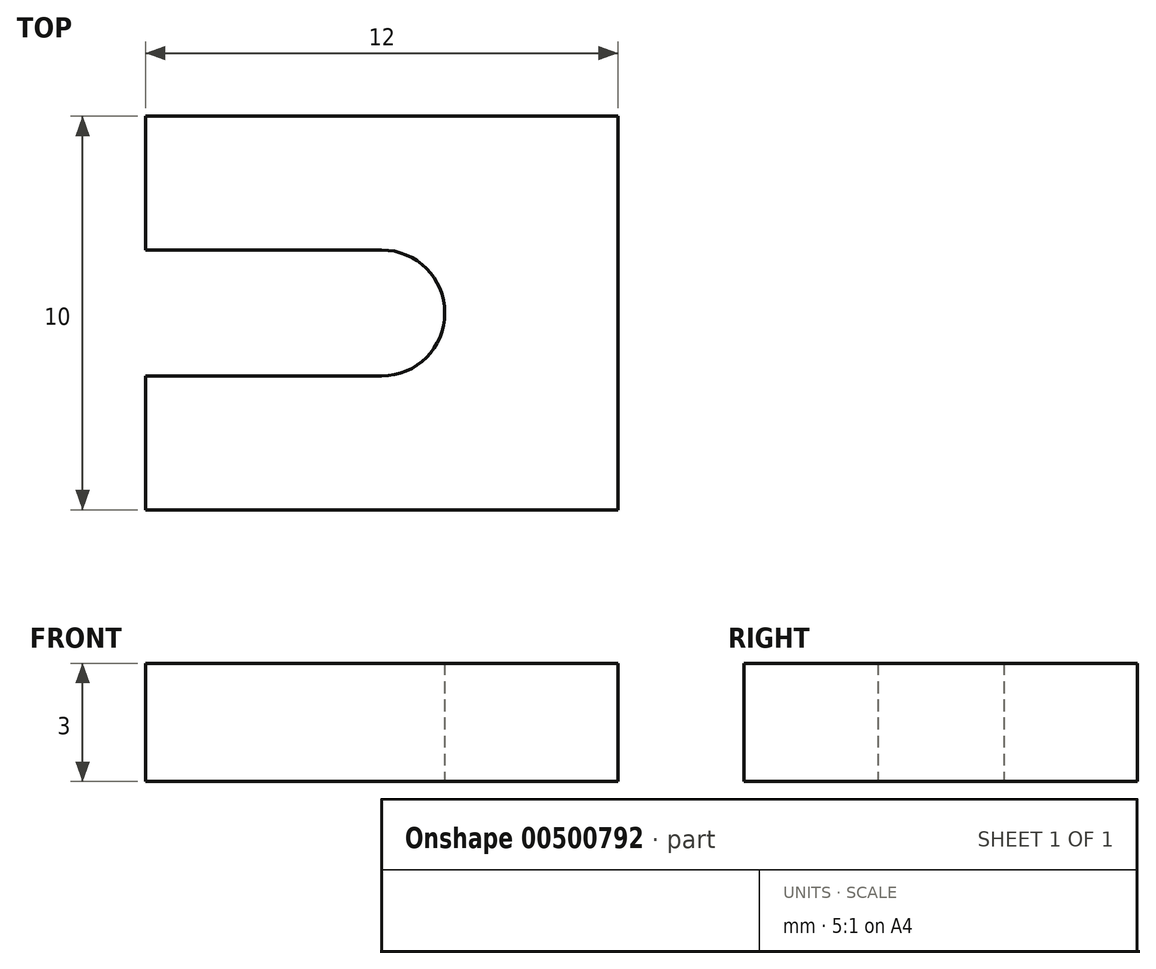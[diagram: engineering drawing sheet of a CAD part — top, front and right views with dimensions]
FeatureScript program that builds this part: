
annotation { "Feature Type Name" : "Feature", "Feature Type Description" : "" }
export const myFeature = defineFeature(function(context is Context, id is Id, definition is map)
    precondition{}
    {
        {
            var Q0;
            Q0=qCreatedBy(makeId("Top.planeOp"),FACE);
            var sketch = newSketch(context, id + "F0", { "sketchPlane" : qUnion([Q0])});
            skLineSegment(sketch, "E0.bottom", {"start": v(6, 5) * mm, "end": v(-6, 5) * mm});
            skLineSegment(sketch, "E0.top", {"start": v(6, -5) * mm, "end": v(-6, -5) * mm});
            skLineSegment(sketch, "E0.left", {"start": v(6, 5) * mm, "end": v(6, -5) * mm});
            skLineSegment(sketch, "E0.right", {"start": v(-6, 5) * mm, "end": v(-6, -5) * mm});
            skPoint(sketch, "E0.middle", {"position": v(0, 0) * mm});
            skCircle(sketch, "E1", {"center": v(0, 0) * mm, "radius": 1.6 * mm});
            skLineSegment(sketch, "E2", {"start": v(0, -1.6) * mm, "end": v(-6, -1.6) * mm});
            skLineSegment(sketch, "E3", {"start": v(-6, -1.6) * mm, "end": v(0, -1.6) * mm});
            skLineSegment(sketch, "E4", {"start": v(0, -1.6) * mm, "end": v(6, -1.6) * mm});
            skLineSegment(sketch, "E5", {"start": v(0, 1.6) * mm, "end": v(-6, 1.6) * mm});
            skLineSegment(sketch, "E6", {"start": v(0, 1.6) * mm, "end": v(6, 1.6) * mm});
            skSolve(sketch);
        }
        {
            var Q0;
            Q0=makeQuery(id+"F0.imprint","IMPRINT",FACE,{"disambiguationData":[TD([[makeQuery(id+"F0.imprint","IMPRINT",EDGE,{"derivedFrom":sQuery(id+"F0.wireOp",EDGE,"E0.bottom")}),1.0]])]});
            var Q1;
            {var subQ0=sQuery(id+"F0.wireOp",EDGE,"E3");Q1=makeQuery(id+"F0.imprint","IMPRINT",FACE,{"disambiguationData":[TD([[makeQuery(id+"F0.imprint","IMPRINT",EDGE,{"derivedFrom":subQ0}),1.0]])]});}
            var Q2;
            {var subQ0=sQuery(id+"F0.wireOp",EDGE,"E4");Q2=makeQuery(id+"F0.imprint","IMPRINT",FACE,{"disambiguationData":[TD([[makeQuery(id+"F0.imprint","IMPRINT",EDGE,{"derivedFrom":subQ0}),1.0]])]});}
            var Q3;
            {var subQ2=sQuery(id+"F0.wireOp",EDGE,"E0.top");Q3=makeQuery(id+"F0.imprint","IMPRINT",FACE,{"disambiguationData":[TD([[makeQuery(id+"F0.imprint","IMPRINT",EDGE,{"derivedFrom":subQ2}),-1.0]])]});}
            extrude(context, id + "F1", {"entities" : qUnion([Q0, Q1, Q2, Q3]), "depth" : 3 * mm, "offsetDistance" : 25 * mm});
        }
    });
